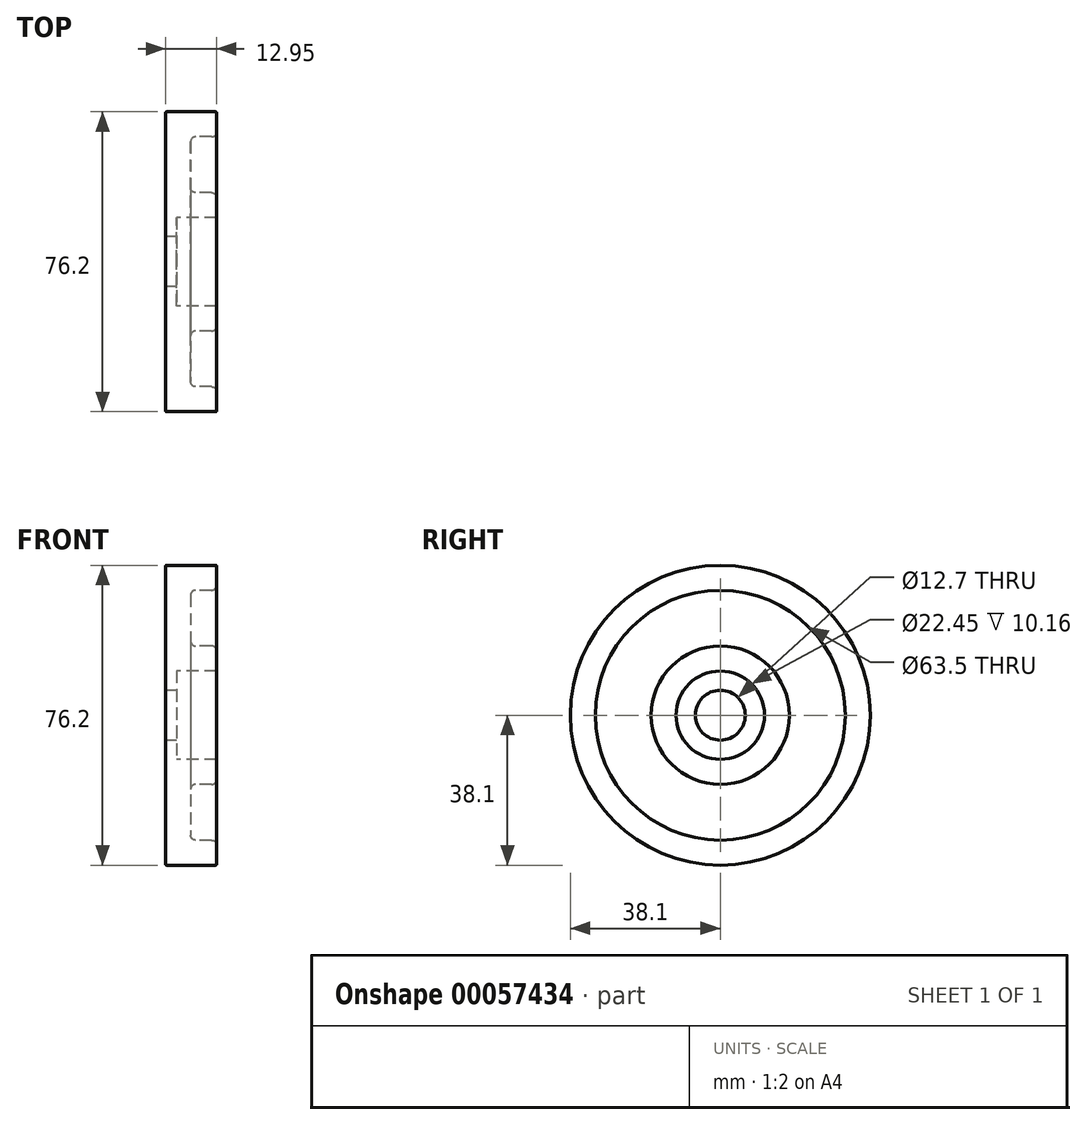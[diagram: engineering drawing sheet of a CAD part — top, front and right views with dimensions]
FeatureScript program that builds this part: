
annotation { "Feature Type Name" : "Feature", "Feature Type Description" : "" }
export const myFeature = defineFeature(function(context is Context, id is Id, definition is map)
    precondition{}
    {
        {
            var Q0;
            Q0=qCreatedBy(makeId("Front.planeOp"),FACE);
            var sketch = newSketch(context, id + "F0", { "sketchPlane" : qUnion([Q0])});
            skLineSegment(sketch, "E0.bottom", {"start": v(0.25, 38.1) * mm, "end": v(12.7, 38.1) * mm});
            skLineSegment(sketch, "E0.left", {"start": v(0, 37.85) * mm, "end": v(0, 6.35) * mm});
            skLineSegment(sketch, "E0.right", {"start": v(12.95, 37.85) * mm, "end": v(12.95, 33.02) * mm});
            skLineSegment(sketch, "E1.bottom", {"start": v(11.68, 31.75) * mm, "end": v(7.62, 31.75) * mm});
            skLineSegment(sketch, "E1.top", {"start": v(11.68, 17.58) * mm, "end": v(7.62, 17.58) * mm});
            skLineSegment(sketch, "E1.right", {"start": v(6.35, 30.48) * mm, "end": v(6.35, 18.85) * mm});
            skLineSegment(sketch, "E2.trimOffspring", {"start": v(12.95, 16.3) * mm, "end": v(12.95, 11.23) * mm});
            skLineSegment(sketch, "E3.bottom", {"start": v(0, 6.35) * mm, "end": v(2.8, 6.35) * mm});
            skLineSegment(sketch, "E4.bottom", {"start": v(12.95, 11.23) * mm, "end": v(2.8, 11.23) * mm});
            skLineSegment(sketch, "E4.right", {"start": v(2.8, 11.23) * mm, "end": v(2.8, 6.35) * mm});
            skPoint(sketch, "E5.visualSharp", {"position": v(0, 38.1) * mm});
            skArc(sketch, "E5.filletArc", {"start": v(0.25, 38.1) * mm, "mid": v(0.07, 38.03) * mm, "end": v(0, 37.85) * mm});
            skPoint(sketch, "E6.visualSharp", {"position": v(12.95, 38.1) * mm});
            skArc(sketch, "E6.filletArc", {"start": v(12.95, 37.85) * mm, "mid": v(12.88, 38.03) * mm, "end": v(12.7, 38.1) * mm});
            skPoint(sketch, "E7.visualSharp", {"position": v(12.95, 31.75) * mm});
            skArc(sketch, "E7.filletArc", {"start": v(11.68, 31.75) * mm, "mid": v(12.58, 32.12) * mm, "end": v(12.95, 33.02) * mm});
            skPoint(sketch, "E8.visualSharp", {"position": v(6.35, 31.75) * mm});
            skArc(sketch, "E8.filletArc", {"start": v(7.62, 31.75) * mm, "mid": v(6.72, 31.38) * mm, "end": v(6.35, 30.48) * mm});
            skPoint(sketch, "E9.visualSharp", {"position": v(6.35, 17.58) * mm});
            skArc(sketch, "E9.filletArc", {"start": v(6.35, 18.85) * mm, "mid": v(6.72, 17.95) * mm, "end": v(7.62, 17.58) * mm});
            skPoint(sketch, "E10.visualSharp", {"position": v(12.95, 17.58) * mm});
            skArc(sketch, "E10.filletArc", {"start": v(12.95, 16.3) * mm, "mid": v(12.58, 17.2) * mm, "end": v(11.68, 17.58) * mm});
            skLineSegment(sketch, "E11", {"start": v(0, 0) * mm, "end": v(46.74, 0) * mm, "construction": true});
            skSolve(sketch);
        }
        {
            var Q0;
            Q0=makeQuery(id+"F0.imprint","IMPRINT",FACE,{"disambiguationData":[TD([[makeQuery(id+"F0.imprint","IMPRINT",EDGE,{"derivedFrom":sQuery(id+"F0.wireOp",EDGE,"E0.bottom")}),-1.0]])]});
            var Q1;
            Q1=sQuery(id+"F0.wireOp",EDGE,"E11");
            revolve(context, id + "F1", {"entities" : qUnion([Q0]), "axis" : qUnion([Q1]), "revolveType" : RevolveType.FULL});
        }
    });
